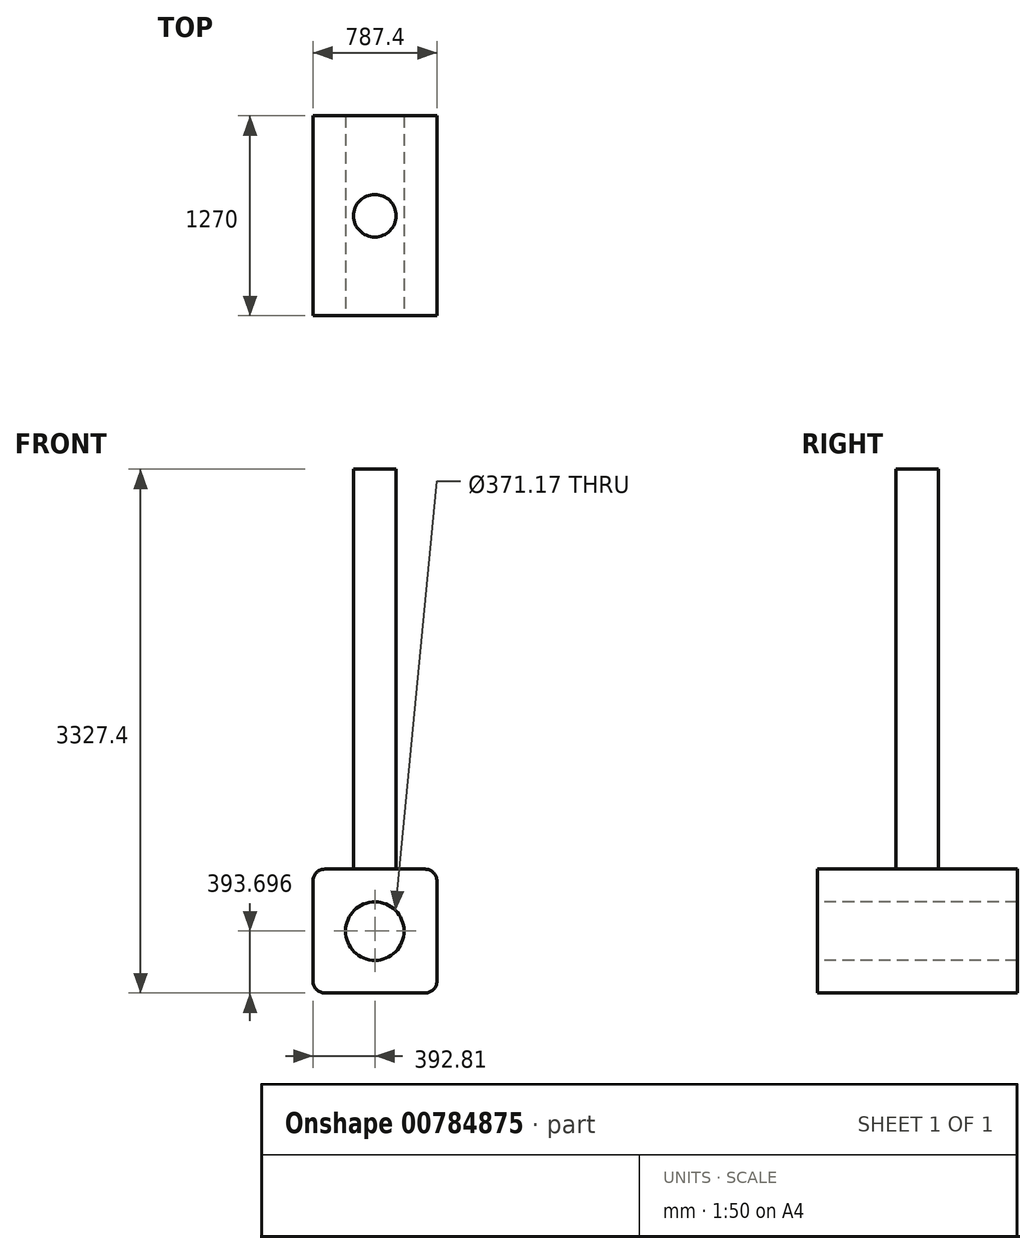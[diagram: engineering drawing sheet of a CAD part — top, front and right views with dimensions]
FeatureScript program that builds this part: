
annotation { "Feature Type Name" : "Feature", "Feature Type Description" : "" }
export const myFeature = defineFeature(function(context is Context, id is Id, definition is map)
    precondition{}
    {
        {
            var Q0;
            Q0=qCreatedBy(makeId("Front.planeOp"),FACE);
            var sketch = newSketch(context, id + "F0", { "sketchPlane" : qUnion([Q0])});
            skLineSegment(sketch, "E0.bottom", {"start": v(-392.81, 311.64) * mm, "end": v(394.59, 311.64) * mm});
            skLineSegment(sketch, "E0.top", {"start": v(-392.81, -475.76) * mm, "end": v(394.59, -475.76) * mm});
            skLineSegment(sketch, "E0.left", {"start": v(-392.81, 311.64) * mm, "end": v(-392.81, -475.76) * mm});
            skLineSegment(sketch, "E0.right", {"start": v(394.59, 311.64) * mm, "end": v(394.59, -475.76) * mm});
            skSolve(sketch);
        }
        {
            var Q0;
            Q0 = qSketchRegion(id + "F0", true);
            extrude(context, id + "F1", {"entities" : qUnion([Q0]), "depth" : 1270 * mm, "offsetDistance" : 25.4 * mm});
        }
        {
            var Q0;
            Q0=makeQuery(id+"F1.opExtrude","SWEPT_EDGE",EDGE,{"disambiguationData":[OSD([sQuery(id+"F0.wireOp",EDGE,"E0.bottom"),sQuery(id+"F0.wireOp",EDGE,"E0.right")])]});
            var Q1;
            Q1=makeQuery(id+"F1.opExtrude","SWEPT_EDGE",EDGE,{"disambiguationData":[OSD([sQuery(id+"F0.wireOp",EDGE,"E0.bottom"),sQuery(id+"F0.wireOp",EDGE,"E0.left")])]});
            var Q2;
            Q2=makeQuery(id+"F1.opExtrude","SWEPT_EDGE",EDGE,{"disambiguationData":[OSD([sQuery(id+"F0.wireOp",EDGE,"E0.top"),sQuery(id+"F0.wireOp",EDGE,"E0.left")])]});
            var Q3;
            Q3=makeQuery(id+"F1.opExtrude","SWEPT_EDGE",EDGE,{"disambiguationData":[OSD([sQuery(id+"F0.wireOp",EDGE,"E0.top"),sQuery(id+"F0.wireOp",EDGE,"E0.right")])]});
            fillet(context, id + "F2", {"entities" : qUnion([Q0, Q1, Q2, Q3]), "radius" : 76.2 * mm, "tangentPropagation" : true, "allowEdgeOverflow" : false});
        }
        {
            var Q0;
            Q0=makeQuery(id+"F1.opExtrude","CAP_FACE",FACE,{"disambiguationData":[OSD([sQuery(id+"F0.wireOp",EDGE,"E0.bottom"),sQuery(id+"F0.wireOp",EDGE,"E0.top"),sQuery(id+"F0.wireOp",EDGE,"E0.left"),sQuery(id+"F0.wireOp",EDGE,"E0.right")])],"isStart":false});
            var sketch = newSketch(context, id + "F3", { "sketchPlane" : qUnion([Q0])});
            skCircle(sketch, "E1", {"center": v(0, -82.06) * mm, "radius": 185.59 * mm});
            skPoint(sketch, "E1.centerSnap0", {"position": v(-392.81, -82.06) * mm});
            skSolve(sketch);
        }
        {
            var Q0;
            Q0 = qSketchRegion(id + "F3", true);
            extrude(context, id + "F4", {"entities" : qUnion([Q0]), "operationType" : NewBodyOperationType.REMOVE, "oppositeDirection" : true, "depth" : 1270 * mm, "offsetDistance" : 25.4 * mm});
        }
        {
            var Q0;
            Q0=makeQuery(id+"F1.opExtrude","SWEPT_FACE",FACE,{"disambiguationData":[OSD([sQuery(id+"F0.wireOp",EDGE,"E0.bottom")])]});
            var sketch = newSketch(context, id + "F5", { "sketchPlane" : qUnion([Q0])});
            skCircle(sketch, "E2", {"center": v(0, -635) * mm, "radius": 135.01 * mm});
            skPoint(sketch, "E2.centerSnap0", {"position": v(-316.61, -635) * mm});
            skSolve(sketch);
        }
        {
            var Q0;
            Q0 = qSketchRegion(id + "F5", true);
            extrude(context, id + "F6", {"entities" : qUnion([Q0]), "operationType" : NewBodyOperationType.ADD, "depth" : 2540 * mm, "offsetDistance" : 25.4 * mm});
        }
    });
